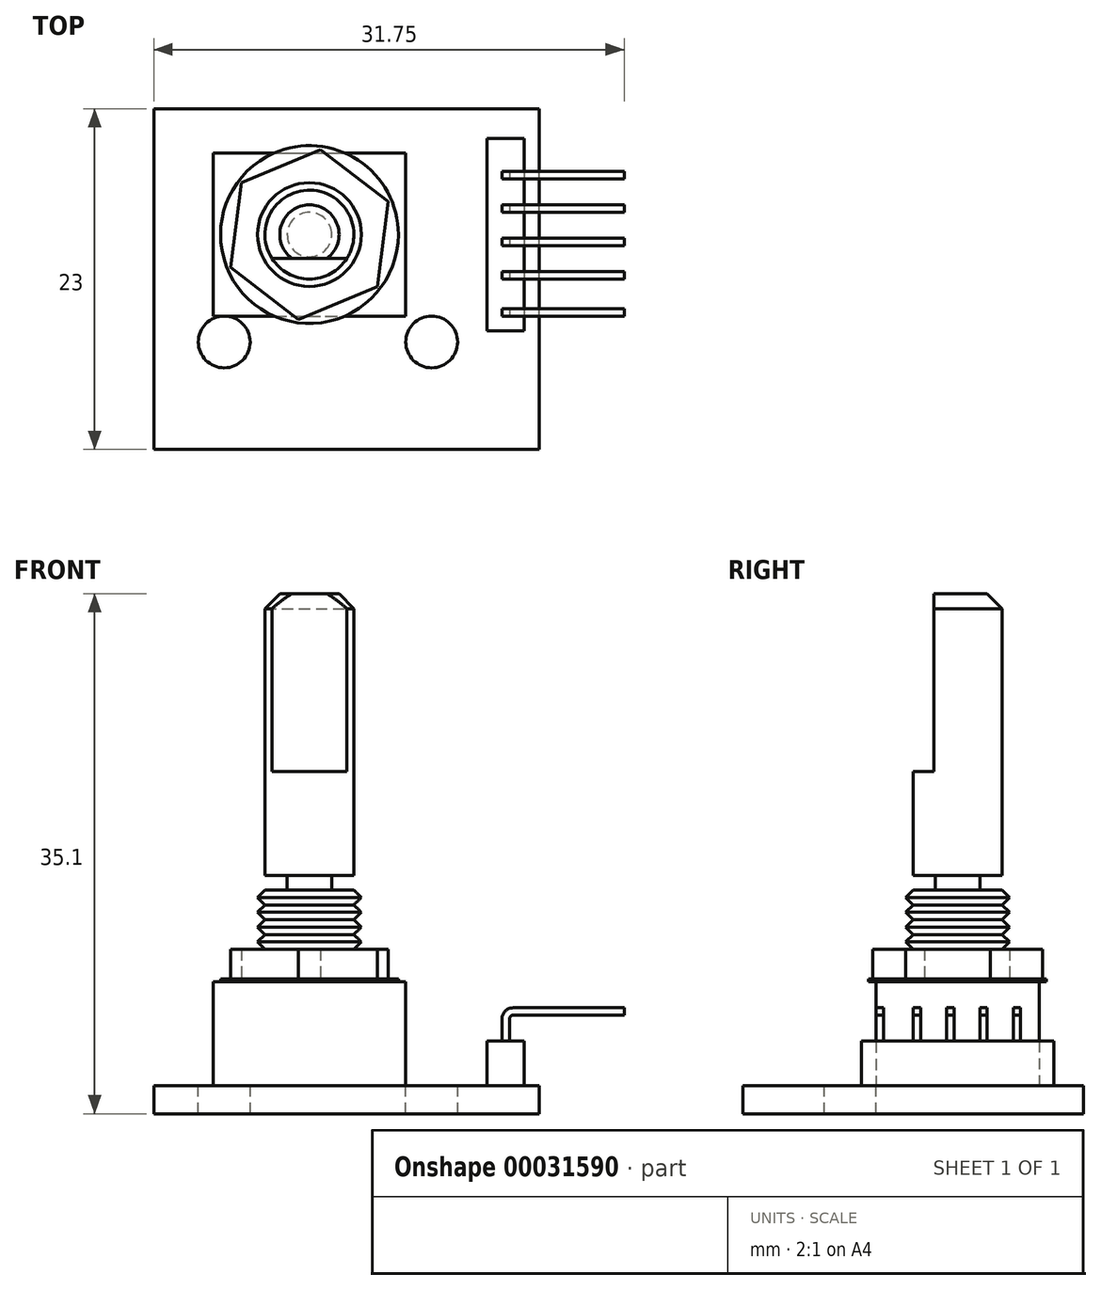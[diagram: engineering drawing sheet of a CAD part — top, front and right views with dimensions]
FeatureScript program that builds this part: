
annotation { "Feature Type Name" : "Feature", "Feature Type Description" : "" }
export const myFeature = defineFeature(function(context is Context, id is Id, definition is map)
    precondition{}
    {
        {
            var Q0;
            Q0=qCreatedBy(makeId("Top.planeOp"),FACE);
            var sketch = newSketch(context, id + "F0", { "sketchPlane" : qUnion([Q0])});
            skLineSegment(sketch, "E0.bottom", {"start": v(0, 0) * mm, "end": v(26, 0) * mm});
            skLineSegment(sketch, "E0.top", {"start": v(0, 23) * mm, "end": v(26, 23) * mm});
            skLineSegment(sketch, "E0.left", {"start": v(0, 0) * mm, "end": v(0, 23) * mm});
            skLineSegment(sketch, "E0.right", {"start": v(26, 0) * mm, "end": v(26, 23) * mm});
            skSolve(sketch);
        }
        {
            var Q0;
            Q0 = qSketchRegion(id + "F0", true);
            extrude(context, id + "F1", {"entities" : qUnion([Q0]), "depth" : 1.9 * mm});
        }
        {
            var Q0;
            Q0=makeQuery(id+"F1.opExtrude","CAP_FACE",FACE,{"disambiguationData":[OSD([sQuery(id+"F0.wireOp",EDGE,"E0.bottom"),sQuery(id+"F0.wireOp",EDGE,"E0.top"),sQuery(id+"F0.wireOp",EDGE,"E0.left"),sQuery(id+"F0.wireOp",EDGE,"E0.right")])],"isStart":false});
            var sketch = newSketch(context, id + "F2", { "sketchPlane" : qUnion([Q0])});
            skSolve(sketch);
        }
        {
            var Q0;
            Q0=makeQuery(id+"F2.imprint","IMPRINT",FACE,{"disambiguationData":[TD([[makeQuery(id+"F2.imprint","IMPRINT",EDGE,{"derivedFrom":makeQuery(id+"F1.opExtrude","CAP_EDGE",EDGE,{"disambiguationData":[OSD([sQuery(id+"F0.wireOp",EDGE,"E0.bottom")])],"isStart":false})}),1.0]])]});
            var sketch = newSketch(context, id + "F3", { "sketchPlane" : qUnion([Q0])});
            skLineSegment(sketch, "E1.bottom", {"start": v(4, 21) * mm, "end": v(17, 21) * mm, "construction": true});
            skLineSegment(sketch, "E1.top", {"start": v(4, 8) * mm, "end": v(17, 8) * mm, "construction": true});
            skLineSegment(sketch, "E1.left", {"start": v(4, 21) * mm, "end": v(4, 8) * mm, "construction": true});
            skLineSegment(sketch, "E1.right", {"start": v(17, 21) * mm, "end": v(17, 8) * mm, "construction": true});
            skLineSegment(sketch, "E2.bottom", {"start": v(4, 20) * mm, "end": v(17, 20) * mm});
            skLineSegment(sketch, "E2.top", {"start": v(4, 9) * mm, "end": v(17, 9) * mm});
            skLineSegment(sketch, "E2.left", {"start": v(4, 20) * mm, "end": v(4, 9) * mm});
            skLineSegment(sketch, "E2.right", {"start": v(17, 20) * mm, "end": v(17, 9) * mm});
            skSolve(sketch);
        }
        {
            var Q0;
            Q0 = qSketchRegion(id + "F3", true);
            extrude(context, id + "F4", {"entities" : qUnion([Q0]), "operationType" : NewBodyOperationType.ADD, "depth" : 7 * mm});
        }
        {
            var Q0;
            Q0=makeQuery(id+"F4.opExtrude","CAP_FACE",FACE,{"disambiguationData":[OSD([sQuery(id+"F3.wireOp",EDGE,"E2.bottom"),sQuery(id+"F3.wireOp",EDGE,"E2.top"),sQuery(id+"F3.wireOp",EDGE,"E2.left"),sQuery(id+"F3.wireOp",EDGE,"E2.right")])],"isStart":false});
            var sketch = newSketch(context, id + "F5", { "sketchPlane" : qUnion([Q0])});
            skCircle(sketch, "E3", {"center": v(10.5, 14.5) * mm, "radius": 6 * mm});
            skSolve(sketch);
        }
        {
            var Q0;
            Q0 = qSketchRegion(id + "F5", true);
            extrude(context, id + "F6", {"entities" : qUnion([Q0]), "operationType" : NewBodyOperationType.ADD, "depth" : 0.2 * mm});
        }
        {
            var Q0;
            Q0=makeQuery(id+"F6.opExtrude","CAP_FACE",FACE,{"disambiguationData":[OSD([sQuery(id+"F5.wireOp",EDGE,"E3")])],"isStart":false});
            var sketch = newSketch(context, id + "F7", { "sketchPlane" : qUnion([Q0])});
            skCircle(sketch, "E4.cCircle", {"center": v(10.5, 14.5) * mm, "radius": 5 * mm, "construction": true});
            skLineSegment(sketch, "E4.0", {"start": v(9.76, 8.77) * mm, "end": v(5.17, 12.28) * mm});
            skLineSegment(sketch, "E4.1", {"start": v(5.17, 12.28) * mm, "end": v(5.91, 18) * mm});
            skLineSegment(sketch, "E4.2", {"start": v(5.91, 18) * mm, "end": v(11.24, 20.23) * mm});
            skLineSegment(sketch, "E4.3", {"start": v(11.24, 20.23) * mm, "end": v(15.83, 16.72) * mm});
            skLineSegment(sketch, "E4.4", {"start": v(15.83, 16.72) * mm, "end": v(15.09, 11) * mm});
            skLineSegment(sketch, "E4.5", {"start": v(15.09, 11) * mm, "end": v(9.76, 8.77) * mm});
            skPoint(sketch, "E4.0.midPoint", {"position": v(7.47, 10.53) * mm});
            skSolve(sketch);
        }
        {
            var Q0;
            Q0 = qSketchRegion(id + "F7", true);
            extrude(context, id + "F8", {"entities" : qUnion([Q0]), "operationType" : NewBodyOperationType.ADD, "depth" : 2 * mm});
        }
        {
            var Q0;
            Q0=makeQuery(id+"F4.opExtrude","SWEPT_FACE",FACE,{"disambiguationData":[OSD([sQuery(id+"F3.wireOp",EDGE,"E2.bottom")])]});
            cPlane(context, id + "F9", {"entities" : qUnion([Q0]), "cplaneType" : CPlaneType.OFFSET, "offset" : 5.5 * mm, "oppositeDirection" : true, "width" : 150 * mm, "height" : 150 * mm});
        }
        {
            var Q0;
            Q0=qCreatedBy(id+"F9.planeOp",FACE);
            var sketch = newSketch(context, id + "F10", { "sketchPlane" : qUnion([Q0])});
            skLineSegment(sketch, "E5", {"start": v(-10.5, 29.73) * mm, "end": v(-10.5, 5.84) * mm, "construction": true});
            skLineSegment(sketch, "E6", {"start": v(-7, 11.6) * mm, "end": v(-7.5, 12.1) * mm});
            skLineSegment(sketch, "E7", {"start": v(-7, 11.6) * mm, "end": v(-7.5, 11.1) * mm});
            skPoint(sketch, "E8.orphan", {"position": v(1, 11.85) * mm});
            skPoint(sketch, "E9.orphan", {"position": v(-15, 11.35) * mm});
            skLineSegment(sketch, "E10", {"start": v(-7.5, 11.1) * mm, "end": v(-10.5, 11.1) * mm});
            skLineSegment(sketch, "E11", {"start": v(-7.5, 12.1) * mm, "end": v(-7, 12.6) * mm});
            skLineSegment(sketch, "E12", {"start": v(-7, 12.6) * mm, "end": v(-7.5, 13.1) * mm});
            skLineSegment(sketch, "E13", {"start": v(-7.5, 13.1) * mm, "end": v(-7, 13.6) * mm});
            skLineSegment(sketch, "E14", {"start": v(-7, 13.6) * mm, "end": v(-7.5, 14.1) * mm});
            skLineSegment(sketch, "E15", {"start": v(-7.5, 14.1) * mm, "end": v(-7, 14.6) * mm});
            skLineSegment(sketch, "E16", {"start": v(-7, 14.6) * mm, "end": v(-7.5, 15.1) * mm});
            skLineSegment(sketch, "E17", {"start": v(-7.5, 15.1) * mm, "end": v(-10.5, 15.1) * mm});
            skLineSegment(sketch, "E18", {"start": v(-10.5, 15.1) * mm, "end": v(-10.5, 11.1) * mm});
            skSolve(sketch);
        }
        {
            var Q0;
            Q0 = qSketchRegion(id + "F10", true);
            var Q1;
            Q1=sQuery(id+"F10.wireOp",EDGE,"E5");
            revolve(context, id + "F11", {"operationType" : NewBodyOperationType.ADD, "entities" : qUnion([Q0]), "axis" : qUnion([Q1]), "revolveType" : RevolveType.FULL});
        }
        {
            var Q0;
            Q0=qCreatedBy(id+"F9.planeOp",FACE);
            var sketch = newSketch(context, id + "F12", { "sketchPlane" : qUnion([Q0])});
            skLineSegment(sketch, "E19", {"start": v(-10.5, 35.1) * mm, "end": v(-10.5, 8.1) * mm});
            skLineSegment(sketch, "E20", {"start": v(-9, 15.1) * mm, "end": v(-9, 16.1) * mm});
            skLineSegment(sketch, "E21", {"start": v(-9, 16.1) * mm, "end": v(-7.5, 16.1) * mm});
            skLineSegment(sketch, "E22", {"start": v(-7.5, 16.1) * mm, "end": v(-7.5, 35.1) * mm});
            skLineSegment(sketch, "E23", {"start": v(-7.5, 35.1) * mm, "end": v(-10.5, 35.1) * mm});
            skLineSegment(sketch, "E24", {"start": v(-9, 15.1) * mm, "end": v(-10.5, 15.1) * mm});
            skSolve(sketch);
        }
        {
            var Q0;
            Q0=makeQuery(id+"F12.imprint","IMPRINT",FACE,{"disambiguationData":[TD([[makeQuery(id+"F12.imprint","IMPRINT",EDGE,{"derivedFrom":sQuery(id+"F12.wireOp",EDGE,"E20")}),1.0]])]});
            var Q1;
            Q1=sQuery(id+"F12.wireOp",EDGE,"E19");
            revolve(context, id + "F13", {"operationType" : NewBodyOperationType.ADD, "entities" : qUnion([Q0]), "axis" : qUnion([Q1]), "revolveType" : RevolveType.FULL});
        }
        {
            var Q0;
            Q0=makeQuery(id+"F13.opRevolve","SWEPT_FACE",FACE,{"disambiguationData":[OSD([sQuery(id+"F12.wireOp",EDGE,"E23")])]});
            var sketch = newSketch(context, id + "F14", { "sketchPlane" : qUnion([Q0])});
            skLineSegment(sketch, "E25.bottom", {"start": v(13.9, 10.86) * mm, "end": v(6.91, 10.86) * mm});
            skLineSegment(sketch, "E25.top", {"start": v(13.9, 12.9) * mm, "end": v(6.91, 12.9) * mm});
            skLineSegment(sketch, "E25.left", {"start": v(13.9, 10.86) * mm, "end": v(13.9, 12.9) * mm});
            skLineSegment(sketch, "E25.right", {"start": v(6.91, 10.86) * mm, "end": v(6.91, 12.9) * mm});
            skSolve(sketch);
        }
        {
            var Q0;
            Q0 = qSketchRegion(id + "F14", true);
            extrude(context, id + "F15", {"entities" : qUnion([Q0]), "operationType" : NewBodyOperationType.REMOVE, "oppositeDirection" : true, "depth" : 12 * mm});
        }
        {
            var Q0;
            Q0=makeQuery(id+"F13.opRevolve","SWEPT_EDGE",EDGE,{"disambiguationData":[OSD([sQuery(id+"F12.wireOp",EDGE,"E22"),sQuery(id+"F12.wireOp",EDGE,"E23")])]});
            chamfer(context, id + "F16", {"entities" : qUnion([Q0]), "width" : 1 * mm, "tangentPropagation" : true});
        }
        {
            var Q0;
            Q0=makeQuery(id+"F2.imprint","IMPRINT",FACE,{"disambiguationData":[TD([[makeQuery(id+"F2.imprint","IMPRINT",EDGE,{"derivedFrom":makeQuery(id+"F1.opExtrude","CAP_EDGE",EDGE,{"disambiguationData":[OSD([sQuery(id+"F0.wireOp",EDGE,"E0.bottom")])],"isStart":false})}),1.0]])]});
            var sketch = newSketch(context, id + "F17", { "sketchPlane" : qUnion([Q0])});
            skLineSegment(sketch, "E26.bottom", {"start": v(22.5, 21) * mm, "end": v(25, 21) * mm});
            skLineSegment(sketch, "E26.top", {"start": v(22.5, 8) * mm, "end": v(25, 8) * mm});
            skLineSegment(sketch, "E26.left", {"start": v(22.5, 21) * mm, "end": v(22.5, 8) * mm});
            skLineSegment(sketch, "E26.right", {"start": v(25, 21) * mm, "end": v(25, 8) * mm});
            skSolve(sketch);
        }
        {
            var Q0;
            Q0 = qSketchRegion(id + "F17", true);
            extrude(context, id + "F18", {"entities" : qUnion([Q0]), "operationType" : NewBodyOperationType.ADD, "depth" : 3 * mm});
        }
        {
            var Q0;
            Q0=makeQuery(id+"F18.opExtrude","SWEPT_FACE",FACE,{"disambiguationData":[OSD([sQuery(id+"F17.wireOp",EDGE,"E26.top")])]});
            cPlane(context, id + "F19", {"entities" : qUnion([Q0]), "cplaneType" : CPlaneType.OFFSET, "offset" : 1.25 * mm, "oppositeDirection" : true, "width" : 150 * mm, "height" : 150 * mm});
        }
        {
            var Q0;
            Q0=makeQuery(id+"F2.imprint","IMPRINT",FACE,{"disambiguationData":[TD([[makeQuery(id+"F2.imprint","IMPRINT",EDGE,{"derivedFrom":makeQuery(id+"F1.opExtrude","CAP_EDGE",EDGE,{"disambiguationData":[OSD([sQuery(id+"F0.wireOp",EDGE,"E0.bottom")])],"isStart":false})}),1.0]])]});
            var sketch = newSketch(context, id + "F20", { "sketchPlane" : qUnion([Q0])});
            skCircle(sketch, "E27", {"center": v(4.75, 7.25) * mm, "radius": 1.75 * mm});
            skCircle(sketch, "E28", {"center": v(18.75, 7.25) * mm, "radius": 1.75 * mm});
            skSolve(sketch);
        }
        {
            var Q0;
            Q0 = qSketchRegion(id + "F20", true);
            extrude(context, id + "F21", {"entities" : qUnion([Q0]), "operationType" : NewBodyOperationType.REMOVE, "oppositeDirection" : true, "depth" : 2 * mm});
        }
        {
            var Q0;
            Q0=qCreatedBy(id+"F19.planeOp",FACE);
            var sketch = newSketch(context, id + "F22", { "sketchPlane" : qUnion([Q0])});
            skLineSegment(sketch, "E29", {"start": v(23.75, 4.9) * mm, "end": v(23.75, 6.4) * mm});
            skLineSegment(sketch, "E30", {"start": v(24.25, 6.9) * mm, "end": v(31.75, 6.9) * mm});
            skPoint(sketch, "E31.visualSharp", {"position": v(23.75, 6.9) * mm});
            skArc(sketch, "E31.filletArc", {"start": v(24.25, 6.9) * mm, "mid": v(23.9, 6.75) * mm, "end": v(23.75, 6.4) * mm});
            skSolve(sketch);
        }
        {
            var Q0;
            Q0=makeQuery(id+"F18.opExtrude","CAP_FACE",FACE,{"disambiguationData":[OSD([sQuery(id+"F17.wireOp",EDGE,"E26.bottom"),sQuery(id+"F17.wireOp",EDGE,"E26.top"),sQuery(id+"F17.wireOp",EDGE,"E26.left"),sQuery(id+"F17.wireOp",EDGE,"E26.right")])],"isStart":false});
            var sketch = newSketch(context, id + "F23", { "sketchPlane" : qUnion([Q0])});
            skLineSegment(sketch, "E32.bottom", {"start": v(23.5, 9.5) * mm, "end": v(24, 9.5) * mm});
            skLineSegment(sketch, "E32.top", {"start": v(23.5, 9) * mm, "end": v(24, 9) * mm});
            skLineSegment(sketch, "E32.left", {"start": v(23.5, 9.5) * mm, "end": v(23.5, 9) * mm});
            skLineSegment(sketch, "E32.right", {"start": v(24, 9.5) * mm, "end": v(24, 9) * mm});
            skSolve(sketch);
        }
        {
            var Q0;
            Q0=makeQuery(id+"F23.imprint","IMPRINT",FACE,{"disambiguationData":[TD([[makeQuery(id+"F23.imprint","IMPRINT",EDGE,{"derivedFrom":sQuery(id+"F23.wireOp",EDGE,"E32.bottom")}),-1.0]])]});
            var Q1;
            Q1=sQuery(id+"F22.wireOp",EDGE,"E29");
            var Q2;
            Q2=sQuery(id+"F22.wireOp",EDGE,"E31.filletArc");
            var Q3;
            Q3=sQuery(id+"F22.wireOp",EDGE,"E30");
            sweep(context, id + "F24", {"operationType" : NewBodyOperationType.ADD, "profiles" : qUnion([Q0]), "path" : qUnion([Q1, Q2, Q3])});
        }
        {
            var Q0;
            Q0=qCreatedBy(id+"F19.planeOp",FACE);
            cPlane(context, id + "F25", {"entities" : qUnion([Q0]), "cplaneType" : CPlaneType.OFFSET, "offset" : 2.25 * mm, "oppositeDirection" : true, "width" : 150 * mm, "height" : 150 * mm});
        }
        {
            var Q0;
            Q0=qCreatedBy(id+"F25.planeOp",FACE);
            var sketch = newSketch(context, id + "F26", { "sketchPlane" : qUnion([Q0])});
            skLineSegment(sketch, "E33.0", {"start": v(23.5, 4.9) * mm, "end": v(23.5, 6.4) * mm});
            skArc(sketch, "E34.0", {"start": v(23.5, 6.4) * mm, "mid": v(23.72, 6.93) * mm, "end": v(24.25, 7.15) * mm});
            skLineSegment(sketch, "E35.0", {"start": v(24.25, 7.15) * mm, "end": v(31.75, 7.15) * mm});
            skLineSegment(sketch, "E36.0", {"start": v(31.75, 7.15) * mm, "end": v(31.75, 6.65) * mm});
            skLineSegment(sketch, "E37.0", {"start": v(24.25, 6.65) * mm, "end": v(31.75, 6.65) * mm});
            skArc(sketch, "E38.0", {"start": v(24, 6.4) * mm, "mid": v(24.07, 6.58) * mm, "end": v(24.25, 6.65) * mm});
            skLineSegment(sketch, "E39.0", {"start": v(24, 4.9) * mm, "end": v(24, 6.4) * mm});
            skLineSegment(sketch, "E40", {"start": v(23.5, 4.9) * mm, "end": v(24, 4.9) * mm});
            skSolve(sketch);
        }
        {
            var Q0;
            Q0 = qSketchRegion(id + "F26", true);
            extrude(context, id + "F27", {"entities" : qUnion([Q0]), "operationType" : NewBodyOperationType.ADD, "oppositeDirection" : true, "depth" : 0.5 * mm});
        }
        {
            var Q0;
            Q0=qCreatedBy(id+"F25.planeOp",FACE);
            cPlane(context, id + "F28", {"entities" : qUnion([Q0]), "cplaneType" : CPlaneType.OFFSET, "offset" : 2.25 * mm, "oppositeDirection" : true, "width" : 150 * mm, "height" : 150 * mm});
        }
        {
            var Q0;
            Q0=qCreatedBy(id+"F28.planeOp",FACE);
            var sketch = newSketch(context, id + "F29", { "sketchPlane" : qUnion([Q0])});
            skLineSegment(sketch, "E41.0", {"start": v(23.5, 4.9) * mm, "end": v(23.5, 6.4) * mm});
            skArc(sketch, "E42.0", {"start": v(23.5, 6.4) * mm, "mid": v(23.72, 6.93) * mm, "end": v(24.25, 7.15) * mm});
            skLineSegment(sketch, "E43.0", {"start": v(24.25, 7.15) * mm, "end": v(31.75, 7.15) * mm});
            skLineSegment(sketch, "E44.0", {"start": v(31.75, 7.15) * mm, "end": v(31.75, 6.65) * mm});
            skLineSegment(sketch, "E45.0", {"start": v(24.25, 6.65) * mm, "end": v(31.75, 6.65) * mm});
            skArc(sketch, "E46.0", {"start": v(24, 6.4) * mm, "mid": v(24.07, 6.58) * mm, "end": v(24.25, 6.65) * mm});
            skLineSegment(sketch, "E47.0", {"start": v(24, 4.9) * mm, "end": v(24, 6.4) * mm});
            skLineSegment(sketch, "E48", {"start": v(23.5, 4.9) * mm, "end": v(24, 4.9) * mm});
            skSolve(sketch);
        }
        {
            var Q0;
            Q0 = qSketchRegion(id + "F29", true);
            extrude(context, id + "F30", {"entities" : qUnion([Q0]), "operationType" : NewBodyOperationType.ADD, "oppositeDirection" : true, "depth" : 0.5 * mm});
        }
        {
            var Q0;
            Q0=qCreatedBy(id+"F28.planeOp",FACE);
            cPlane(context, id + "F31", {"entities" : qUnion([Q0]), "cplaneType" : CPlaneType.OFFSET, "offset" : 2.25 * mm, "oppositeDirection" : true, "width" : 150 * mm, "height" : 150 * mm});
        }
        {
            var Q0;
            Q0=qCreatedBy(id+"F31.planeOp",FACE);
            var sketch = newSketch(context, id + "F32", { "sketchPlane" : qUnion([Q0])});
            skLineSegment(sketch, "E49.0", {"start": v(24.25, 7.15) * mm, "end": v(31.75, 7.15) * mm});
            skArc(sketch, "E50.0", {"start": v(23.5, 6.4) * mm, "mid": v(23.72, 6.93) * mm, "end": v(24.25, 7.15) * mm});
            skLineSegment(sketch, "E51.0", {"start": v(23.5, 4.9) * mm, "end": v(23.5, 6.4) * mm});
            skLineSegment(sketch, "E52.0", {"start": v(24, 4.9) * mm, "end": v(24, 6.4) * mm});
            skArc(sketch, "E53.0", {"start": v(24, 6.4) * mm, "mid": v(24.07, 6.58) * mm, "end": v(24.25, 6.65) * mm});
            skLineSegment(sketch, "E54.0", {"start": v(24.25, 6.65) * mm, "end": v(31.75, 6.65) * mm});
            skLineSegment(sketch, "E55.0", {"start": v(31.75, 7.15) * mm, "end": v(31.75, 6.65) * mm});
            skLineSegment(sketch, "E56", {"start": v(23.5, 4.9) * mm, "end": v(24, 4.9) * mm});
            skSolve(sketch);
        }
        {
            var Q0;
            Q0 = qSketchRegion(id + "F32", true);
            extrude(context, id + "F33", {"entities" : qUnion([Q0]), "operationType" : NewBodyOperationType.ADD, "oppositeDirection" : true, "depth" : 0.5 * mm});
        }
        {
            var Q0;
            Q0=qCreatedBy(id+"F31.planeOp",FACE);
            cPlane(context, id + "F34", {"entities" : qUnion([Q0]), "cplaneType" : CPlaneType.OFFSET, "offset" : 2.25 * mm, "oppositeDirection" : true, "width" : 150 * mm, "height" : 150 * mm});
        }
        {
            var Q0;
            Q0=qCreatedBy(id+"F34.planeOp",FACE);
            var sketch = newSketch(context, id + "F35", { "sketchPlane" : qUnion([Q0])});
            skLineSegment(sketch, "E57.0", {"start": v(24.25, 6.65) * mm, "end": v(31.75, 6.65) * mm});
            skLineSegment(sketch, "E58.0", {"start": v(24.25, 7.15) * mm, "end": v(31.75, 7.15) * mm});
            skArc(sketch, "E59.0", {"start": v(23.5, 6.4) * mm, "mid": v(23.72, 6.93) * mm, "end": v(24.25, 7.15) * mm});
            skLineSegment(sketch, "E60.0", {"start": v(23.5, 4.9) * mm, "end": v(23.5, 6.4) * mm});
            skLineSegment(sketch, "E61.0", {"start": v(24, 4.9) * mm, "end": v(24, 6.4) * mm});
            skArc(sketch, "E62.0", {"start": v(24, 6.4) * mm, "mid": v(24.07, 6.58) * mm, "end": v(24.25, 6.65) * mm});
            skLineSegment(sketch, "E63.0", {"start": v(31.75, 7.15) * mm, "end": v(31.75, 6.65) * mm});
            skLineSegment(sketch, "E64", {"start": v(23.5, 4.9) * mm, "end": v(24, 4.9) * mm});
            skSolve(sketch);
        }
        {
            var Q0;
            Q0 = qSketchRegion(id + "F35", true);
            extrude(context, id + "F36", {"entities" : qUnion([Q0]), "operationType" : NewBodyOperationType.ADD, "oppositeDirection" : true, "depth" : 0.5 * mm});
        }
    });
